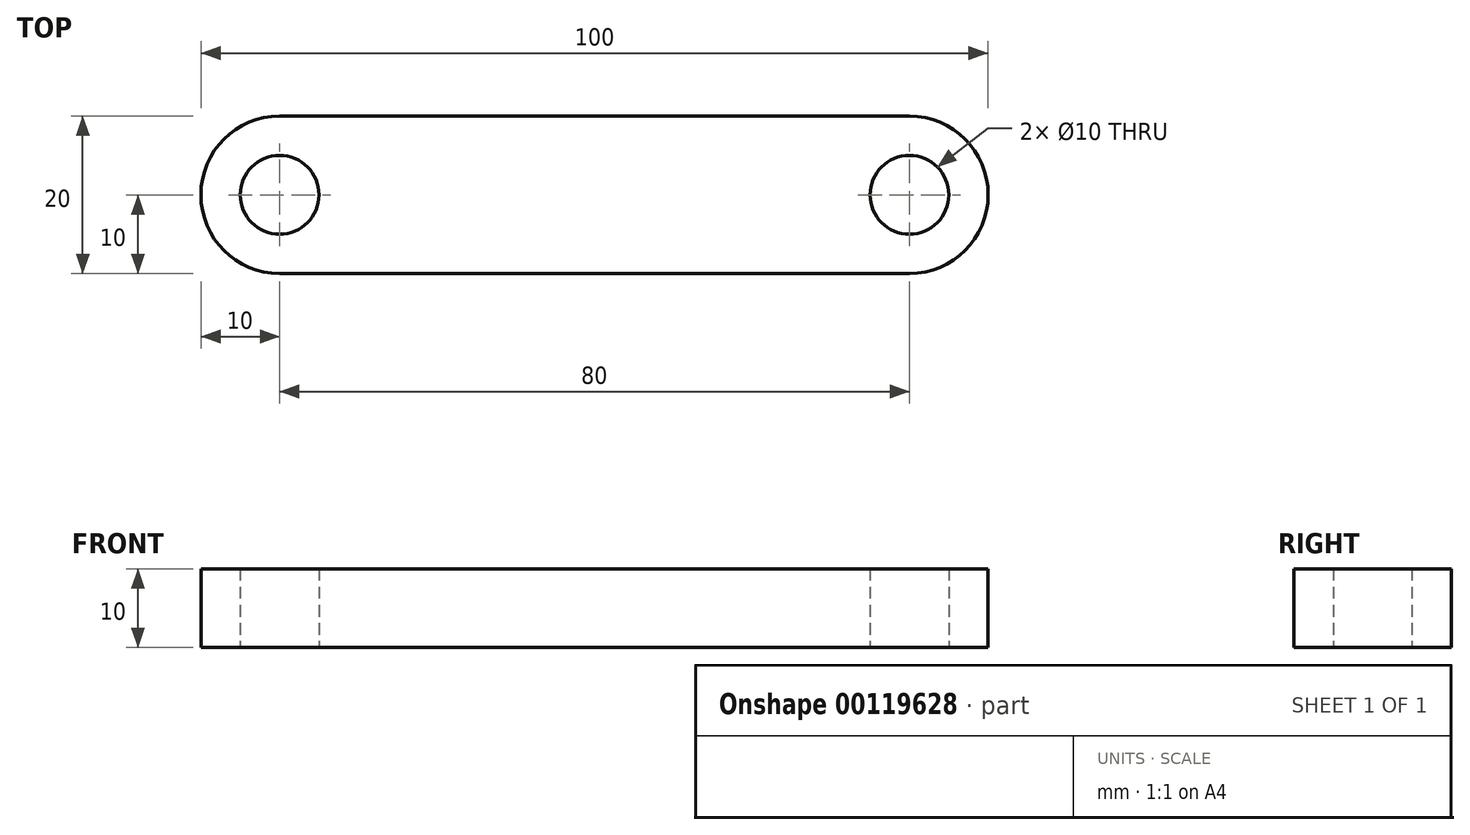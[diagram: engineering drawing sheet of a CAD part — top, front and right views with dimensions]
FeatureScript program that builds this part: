
annotation { "Feature Type Name" : "Feature", "Feature Type Description" : "" }
export const myFeature = defineFeature(function(context is Context, id is Id, definition is map)
    precondition{}
    {
        {
            var Q0;
            Q0=qCreatedBy(makeId("Top.planeOp"),FACE);
            var sketch = newSketch(context, id + "F0", { "sketchPlane" : qUnion([Q0])});
            skLineSegment(sketch, "E0", {"start": v(0, 20) * mm, "end": v(80, 20) * mm});
            skLineSegment(sketch, "E1", {"start": v(80, 0) * mm, "end": v(0, 0) * mm});
            skArc(sketch, "E2", {"start": v(0, 20) * mm, "mid": v(-10, 10) * mm, "end": v(0, 0) * mm});
            skArc(sketch, "E3", {"start": v(80, 0) * mm, "mid": v(90, 10) * mm, "end": v(80, 20) * mm});
            skCircle(sketch, "E4", {"center": v(0, 10) * mm, "radius": 5 * mm});
            skCircle(sketch, "E5", {"center": v(80, 10) * mm, "radius": 5 * mm});
            skSolve(sketch);
        }
        {
            var Q0;
            Q0=makeQuery(id+"F0.imprint","IMPRINT",FACE,{"disambiguationData":[TD([[makeQuery(id+"F0.imprint","IMPRINT",EDGE,{"derivedFrom":sQuery(id+"F0.wireOp",EDGE,"E0")}),-1.0]])]});
            extrude(context, id + "F1", {"entities" : qUnion([Q0]), "depth" : 10 * mm});
        }
    });
